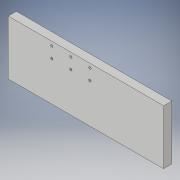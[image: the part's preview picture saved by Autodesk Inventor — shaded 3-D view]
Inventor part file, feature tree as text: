
AUTODESK INVENTOR PART (.ipt)
format: ipt  version: 2018 (Build 220112000, 112)  size: 107,008 bytes
history: native  units: in
note: dims shown in document units (in); Inventor stores cm internally (conversion verified against a paired STEP export)
features: extrude x2, sketch x2
ambient origin geometry x8: Origin, YZ Plane, XZ Plane, XY Plane, X Axis, Y Axis, Z Axis, Center Point
bodies: Solid1 (feature_tree)
feature tree (4):
  extrude  "Extrusion1"  Depth=5.0in
  extrude  "Extrusion2"  Depth=0.75in
  sketch  "Sketch1"  dims[d0=14.25in d1=5.0in]
  sketch  "Sketch2"  dims[d2=0.75in d3=0.0in d4=4.0in d5=0.375in d6=1.75in d7=1.75in d8=1.0in d9=0.21in d10=0.75in d11=0.0in]
